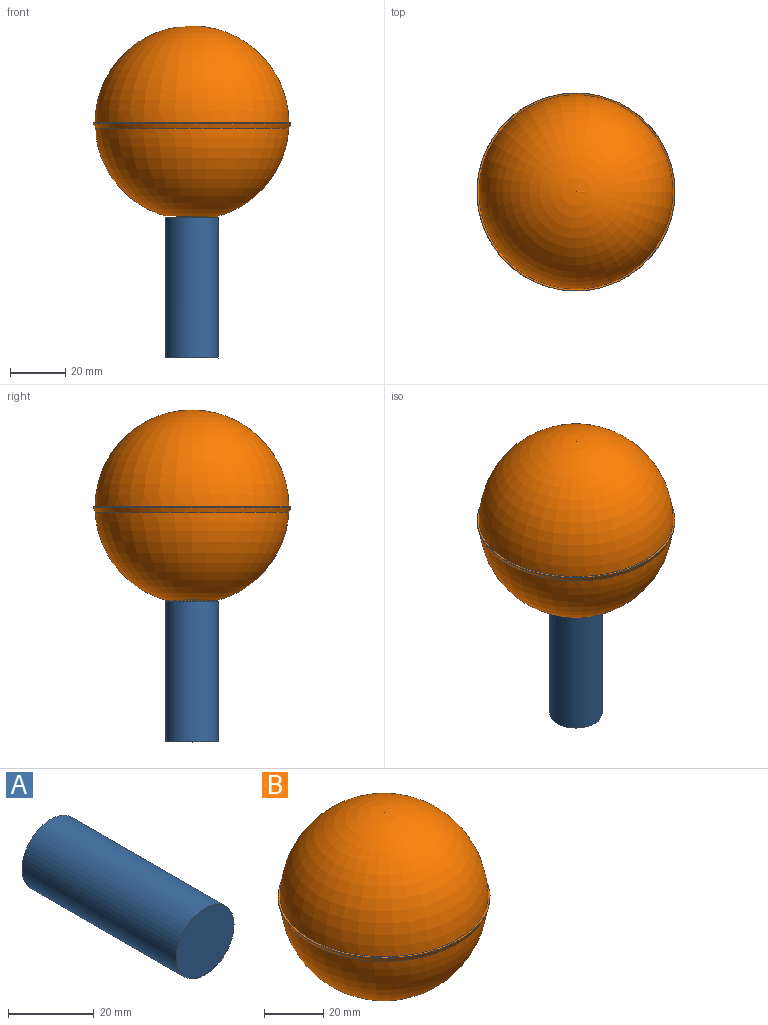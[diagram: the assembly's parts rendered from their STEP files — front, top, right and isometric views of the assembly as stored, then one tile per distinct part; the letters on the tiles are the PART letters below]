
ASSEMBLY  parts=2 mates=1
PART A: 3 faces, bbox 19.1x50.8x19.1 mm
  f0: cylinder r=9.53mm len=50.8mm, axis (0,1,0), area 3040.2mm2, adj f1,f2
  f1: plane 19.05x19.05mm, normal (0,-1,0), area 285mm2, adj f0
  f2: plane 19.05x19.05mm, normal (0,1,0), area 285mm2, adj f0
PART B: 8 faces, bbox 71.4x71.4x70.4 mm
  f0: revolved ~71.35x71.35mm, area 183.1mm2, adj f1,f4
  f1: torus R=0.03mm, axis (0,0,1), area 7667.5mm2, adj f0
  f2: torus R=0.03mm, axis (0,0,1), area 6979.1mm2, adj f3,f5
  f3: revolved ~71.35x71.35mm, area 437.1mm2, adj f2,f4
  f4: cone r=35.68mm half-angle=0deg, axis (0,0,-1), area 29.1mm2, adj f0,f3
  f5: sphere r=9.53mm, area 435.7mm2, adj f2
  f6: torus R=0.03mm, axis (0,0,1), area 12285.5mm2, adj f7
  f7: sphere r=12.7mm, area 521mm2, adj f6
PLACE A rot(axis=(1,0,0),90deg) t=(47.22,-10.08,-1.9)mm
PLACE B t=(11.52,-10.08,-3.88)mm
MATE fastened A.f0 <-> B.f4  axis (0,0,1) through (47.22,-10.08,-1.9)mm
